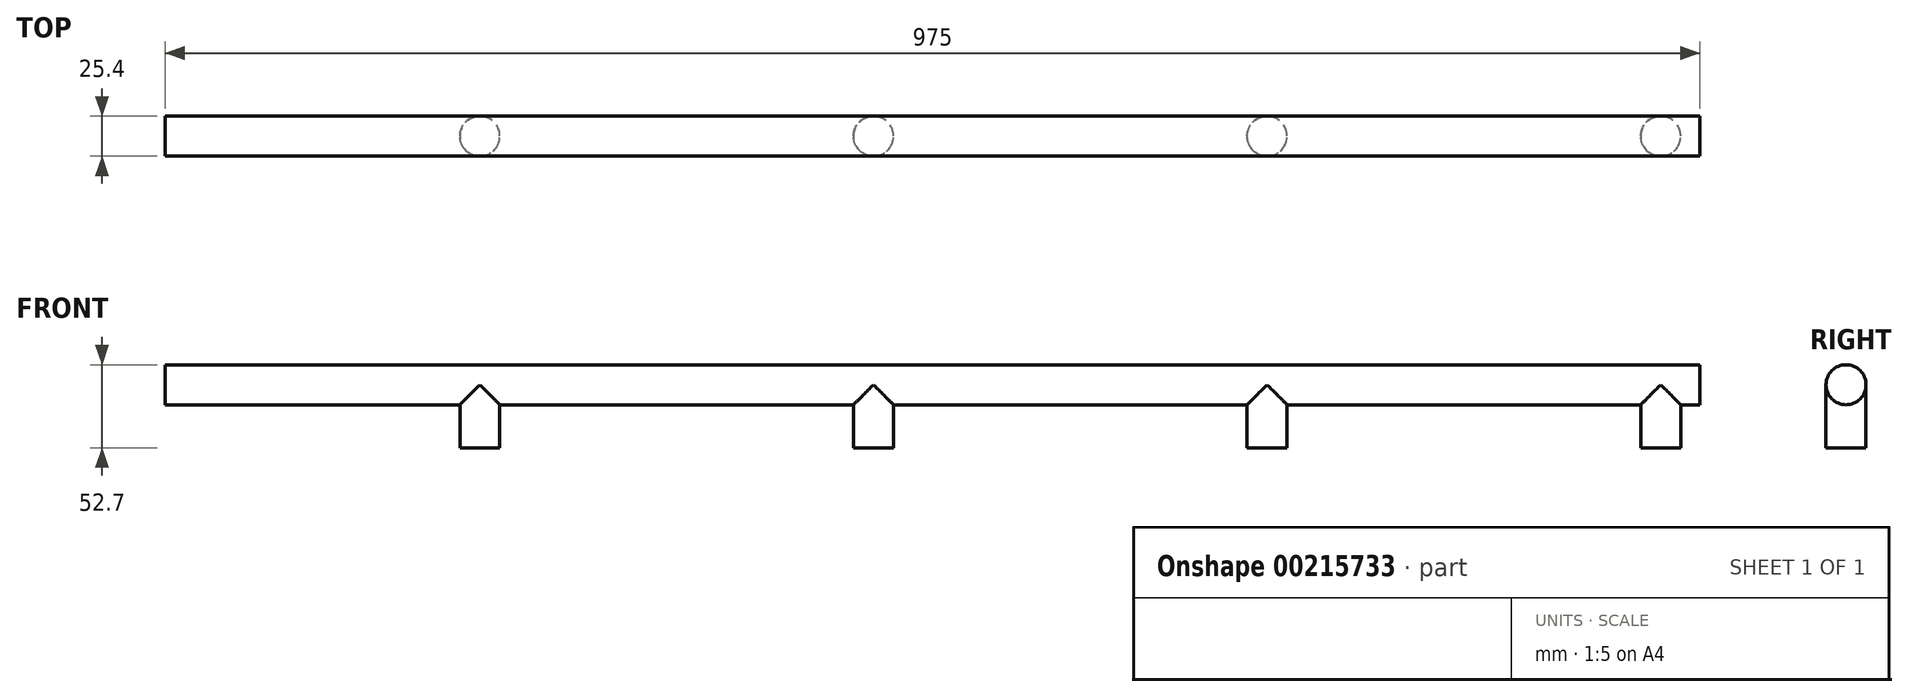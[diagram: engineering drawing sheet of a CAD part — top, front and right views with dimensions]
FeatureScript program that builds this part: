
annotation { "Feature Type Name" : "Feature", "Feature Type Description" : "" }
export const myFeature = defineFeature(function(context is Context, id is Id, definition is map)
    precondition{}
    {
        {
            var Q0;
            Q0=qCreatedBy(makeId("Right.planeOp"),FACE);
            var sketch = newSketch(context, id + "F0", { "sketchPlane" : qUnion([Q0])});
            skCircle(sketch, "E0", {"center": v(0, 0) * mm, "radius": 12.7 * mm});
            skSolve(sketch);
        }
        {
            var Q0;
            Q0 = qSketchRegion(id + "F0", true);
            extrude(context, id + "F1", {"entities" : qUnion([Q0]), "oppositeDirection" : true, "depth" : 1200 * mm});
        }
        {
            var Q0;
            Q0=qCreatedBy(makeId("Top.planeOp"),FACE);
            var sketch = newSketch(context, id + "F2", { "sketchPlane" : qUnion([Q0])});
            skCircle(sketch, "E1", {"center": v(-250, 0) * mm, "radius": 12.7 * mm});
            skCircle(sketch, "E2", {"center": v(-500, 0) * mm, "radius": 12.7 * mm});
            skCircle(sketch, "E3", {"center": v(-750, 0) * mm, "radius": 12.7 * mm});
            skCircle(sketch, "E4", {"center": v(-1000, 0) * mm, "radius": 12.7 * mm});
            skSolve(sketch);
        }
        {
            var Q0;
            Q0 = qSketchRegion(id + "F2", true);
            extrude(context, id + "F3", {"entities" : qUnion([Q0]), "operationType" : NewBodyOperationType.ADD, "oppositeDirection" : true, "depth" : 40 * mm});
        }
        {
            var Q0;
            Q0=makeQuery(id+"F1.opExtrude","CAP_FACE",FACE,{"disambiguationData":[OSD([sQuery(id+"F0.wireOp",EDGE,"E0")])],"isStart":true});
            extrude(context, id + "F4", {"entities" : qUnion([Q0]), "operationType" : NewBodyOperationType.REMOVE, "oppositeDirection" : true, "depth" : 225 * mm});
        }
    });
